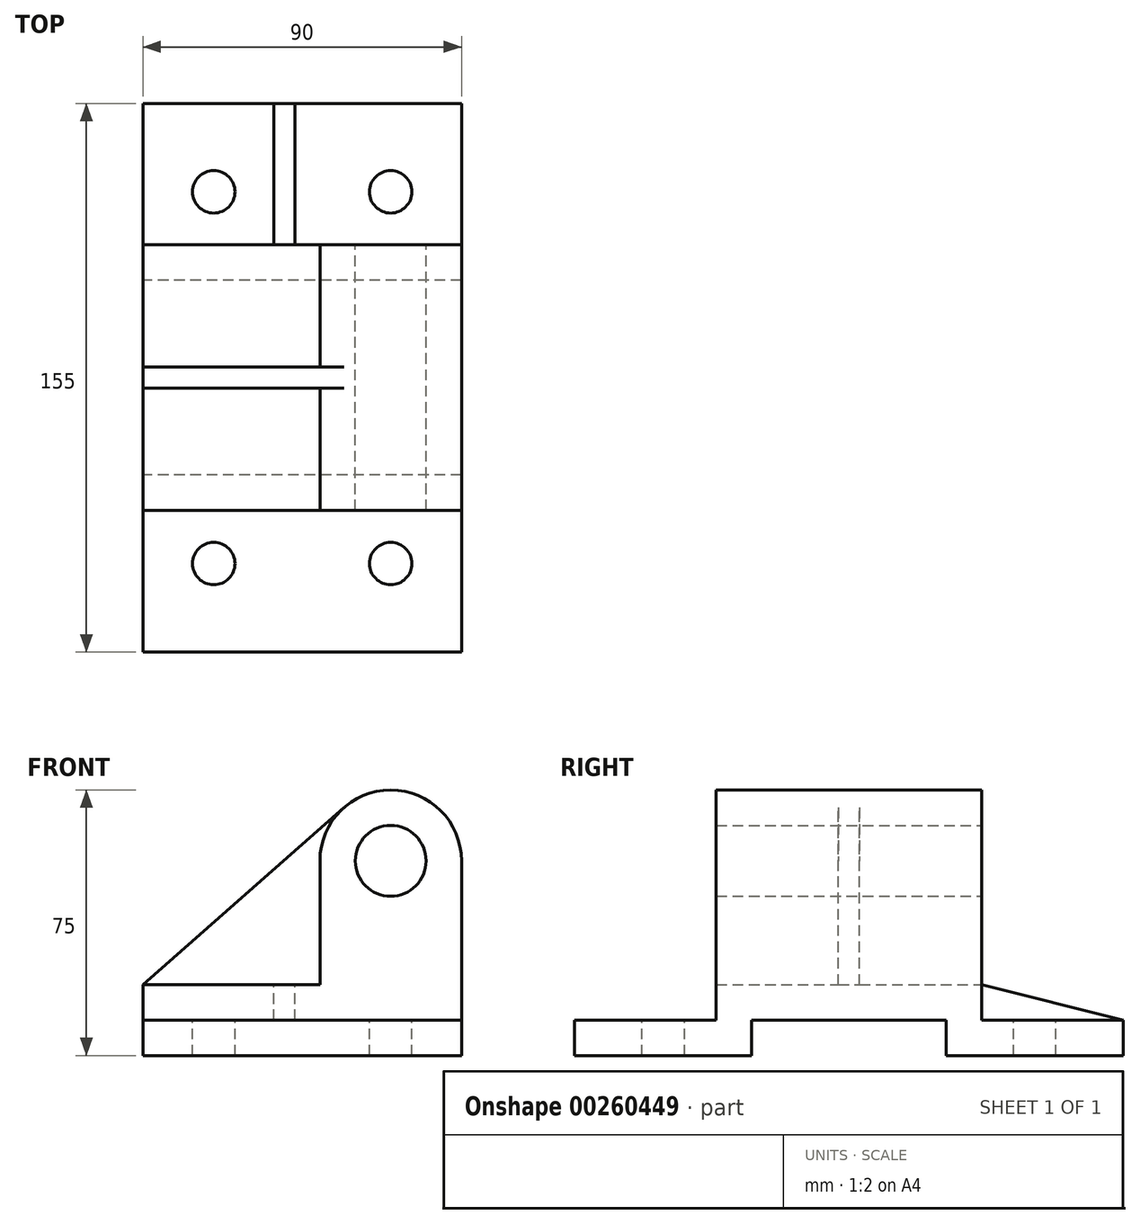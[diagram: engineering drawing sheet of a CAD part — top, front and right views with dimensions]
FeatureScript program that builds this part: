
annotation { "Feature Type Name" : "Feature", "Feature Type Description" : "" }
export const myFeature = defineFeature(function(context is Context, id is Id, definition is map)
    precondition{}
    {
        {
            var Q0;
            Q0=qCreatedBy(makeId("Right.planeOp"),FACE);
            var sketch = newSketch(context, id + "F0", { "sketchPlane" : qUnion([Q0])});
            skLineSegment(sketch, "E0", {"start": v(77.5, -20) * mm, "end": v(77.5, -10) * mm});
            skLineSegment(sketch, "E1", {"start": v(-77.5, -20) * mm, "end": v(-77.5, -10) * mm});
            skLineSegment(sketch, "E2", {"start": v(-77.5, -10) * mm, "end": v(-37.5, -10) * mm});
            skLineSegment(sketch, "E3", {"start": v(77.5, -10) * mm, "end": v(37.5, -10) * mm});
            skLineSegment(sketch, "E4", {"start": v(-27.5, -20) * mm, "end": v(-27.5, -10) * mm});
            skLineSegment(sketch, "E5", {"start": v(27.5, -20) * mm, "end": v(27.5, -10) * mm});
            skLineSegment(sketch, "E6", {"start": v(-77.5, -20) * mm, "end": v(-27.5, -20) * mm});
            skLineSegment(sketch, "E7", {"start": v(27.5, -20) * mm, "end": v(77.5, -20) * mm});
            skLineSegment(sketch, "E8", {"start": v(-37.5, -10) * mm, "end": v(-37.5, 0) * mm});
            skLineSegment(sketch, "E9", {"start": v(37.5, -10) * mm, "end": v(37.5, 0) * mm});
            skLineSegment(sketch, "E10", {"start": v(-37.5, 0) * mm, "end": v(37.5, 0) * mm});
            skLineSegment(sketch, "E11", {"start": v(-27.5, -10) * mm, "end": v(27.5, -10) * mm});
            skSolve(sketch);
        }
        {
            var Q0;
            Q0 = qSketchRegion(id + "F0", true);
            extrude(context, id + "F1", {"entities" : qUnion([Q0]), "endBound" : BoundingType.SYMMETRIC, "depth" : 90 * mm});
        }
        {
            var Q0;
            Q0=makeQuery(id+"F1.opExtrude","SWEPT_FACE",FACE,{"disambiguationData":[OSD([sQuery(id+"F0.wireOp",EDGE,"E2")])]});
            var sketch = newSketch(context, id + "F2", { "sketchPlane" : qUnion([Q0])});
            skCircle(sketch, "E12", {"center": v(25, -52.5) * mm, "radius": 6 * mm});
            skCircle(sketch, "E13", {"center": v(-25, -52.5) * mm, "radius": 6 * mm});
            skLineSegment(sketch, "E14", {"start": v(0, 0) * mm, "end": v(-92.1, 0) * mm, "construction": true});
            skCircle(sketch, "E15.MirrorC", {"center": v(-25, 52.5) * mm, "radius": 6 * mm});
            skCircle(sketch, "E16.MirrorC", {"center": v(25, 52.5) * mm, "radius": 6 * mm});
            skSolve(sketch);
        }
        {
            var Q0;
            Q0 = qSketchRegion(id + "F2", true);
            extrude(context, id + "F3", {"entities" : qUnion([Q0]), "operationType" : NewBodyOperationType.REMOVE, "endBound" : BoundingType.THROUGH_ALL, "oppositeDirection" : true, "depth" : 25 * mm});
        }
        {
            var Q0;
            Q0=makeQuery(id+"F1.opExtrude","CAP_FACE",FACE,{"disambiguationData":[OSD([sQuery(id+"F0.wireOp",EDGE,"E0"),sQuery(id+"F0.wireOp",EDGE,"E1"),sQuery(id+"F0.wireOp",EDGE,"E2"),sQuery(id+"F0.wireOp",EDGE,"E3"),sQuery(id+"F0.wireOp",EDGE,"E4"),sQuery(id+"F0.wireOp",EDGE,"E5"),sQuery(id+"F0.wireOp",EDGE,"E6"),sQuery(id+"F0.wireOp",EDGE,"E7"),sQuery(id+"F0.wireOp",EDGE,"E8"),sQuery(id+"F0.wireOp",EDGE,"E9"),sQuery(id+"F0.wireOp",EDGE,"E10"),sQuery(id+"F0.wireOp",EDGE,"E11")])],"isStart":true});
            cPlane(context, id + "F4", {"entities" : qUnion([Q0]), "cplaneType" : CPlaneType.OFFSET, "offset" : 37 * mm, "oppositeDirection" : true, "width" : 150 * mm, "height" : 150 * mm});
        }
        {
            var Q0;
            Q0=qCreatedBy(id+"F4.planeOp",FACE);
            var sketch = newSketch(context, id + "F5", { "sketchPlane" : qUnion([Q0])});
            skLineSegment(sketch, "E17", {"start": v(-37.5, 0) * mm, "end": v(-77.5, -10) * mm});
            skLineSegment(sketch, "E18", {"start": v(-77.5, -10) * mm, "end": v(-37.5, -10) * mm});
            skLineSegment(sketch, "E19", {"start": v(-37.5, -10) * mm, "end": v(-37.5, 0) * mm});
            skSolve(sketch);
        }
        {
            var Q0;
            Q0 = qSketchRegion(id + "F5", true);
            extrude(context, id + "F6", {"entities" : qUnion([Q0]), "operationType" : NewBodyOperationType.ADD, "oppositeDirection" : true, "depth" : 6 * mm});
        }
        {
            var Q0;
            Q0=qCreatedBy(makeId("Front.planeOp"),FACE);
            var sketch = newSketch(context, id + "F7", { "sketchPlane" : qUnion([Q0])});
            skLineSegment(sketch, "E20", {"start": v(45, 0) * mm, "end": v(5, 0) * mm});
            skLineSegment(sketch, "E21", {"start": v(5, 0) * mm, "end": v(5, 35) * mm});
            skLineSegment(sketch, "E22", {"start": v(45, 0) * mm, "end": v(45, 35) * mm});
            skArc(sketch, "E23", {"start": v(45, 35) * mm, "mid": v(25, 55) * mm, "end": v(5, 35) * mm});
            skCircle(sketch, "E24", {"center": v(25, 35) * mm, "radius": 10 * mm});
            skSolve(sketch);
        }
        {
            var Q0;
            Q0 = qSketchRegion(id + "F7", true);
            var Q1;
            {var subQ2=sQuery(id+"F5.wireOp",EDGE,"E17");var subQ3=sQuery(id+"F0.wireOp",EDGE,"E8");Q1=makeQuery(id+"FYlY6qY9incRTqu_1.1.F6.boolean.opBoolean","SPLIT",FACE,{"disambiguationData":[TD([makeQuery(id+"FYlY6qY9incRTqu_1.1.F6.opExtrude","CAP_FACE",FACE,{"disambiguationData":[OSD([subQ2,sQuery(id+"F5.wireOp",EDGE,"E18"),sQuery(id+"F5.wireOp",EDGE,"E19")])],"isStart":false})])],"derivedFrom":makeQuery(id+"F1.opExtrude","SWEPT_FACE",FACE,{"disambiguationData":[OSD([subQ3])]})});}
            var Q2;
            {var subQ0=sQuery(id+"F5.wireOp",EDGE,"E17");var subQ3=sQuery(id+"F0.wireOp",EDGE,"E9");Q2=makeQuery(id+"F6.boolean.opBoolean","SPLIT",FACE,{"disambiguationData":[TD([makeQuery(id+"F6.opExtrude","CAP_FACE",FACE,{"disambiguationData":[OSD([subQ0,sQuery(id+"F5.wireOp",EDGE,"E18"),sQuery(id+"F5.wireOp",EDGE,"E19")])],"isStart":false})])],"derivedFrom":makeQuery(id+"F1.opExtrude","SWEPT_FACE",FACE,{"disambiguationData":[OSD([subQ3])]})});}
            extrude(context, id + "F8", {"entities" : qUnion([Q0]), "operationType" : NewBodyOperationType.ADD, "endBound" : BoundingType.SYMMETRIC, "endBoundEntityFace" : qUnion([Q1]), "depth" : 75 * mm});
        }
        {
            var Q0;
            Q0=qCreatedBy(makeId("Front.planeOp"),FACE);
            var sketch = newSketch(context, id + "F9", { "sketchPlane" : qUnion([Q0])});
            skLineSegment(sketch, "E25", {"start": v(-45, 0) * mm, "end": v(11.78, 50) * mm});
            skLineSegment(sketch, "E26", {"start": v(5, 0) * mm, "end": v(-45, 0) * mm});
            skLineSegment(sketch, "E27", {"start": v(11.78, 50) * mm, "end": v(5, 0) * mm});
            skSolve(sketch);
        }
        {
            var Q0;
            Q0 = qSketchRegion(id + "F9", true);
            extrude(context, id + "F10", {"entities" : qUnion([Q0]), "operationType" : NewBodyOperationType.ADD, "endBound" : BoundingType.SYMMETRIC, "depth" : 6 * mm});
        }
    });
